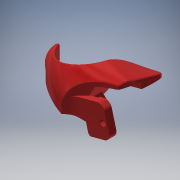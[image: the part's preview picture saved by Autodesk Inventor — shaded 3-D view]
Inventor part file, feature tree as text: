
AUTODESK INVENTOR PART (.ipt)
format: ipt  version: 2018 (Build 220112000, 112)  size: 882,688 bytes
history: native  units: mm
features: other x8, extrude x1, fillet x1, sketch x1, reference x1
ambient origin geometry x8: Origin, YZ Plane, XZ Plane, XY Plane, X Axis, Y Axis, Z Axis, Center Point
bodies: Body1 (feature_tree)
feature tree (12):
  other  "ソリッド1"
  other  "ダイレクト編集1"
  extrude  "押し出し1"  Depth=8.8365mm
  fillet  "フィレット1"  Radius=0.5mm
  sketch  "スケッチ1"
  reference  "参照1"
  other  "尺度1"
  other  "削除1"
  other  "削除2"
  parser-record x1  (decoder bookkeeping rows leaked as tree rows — omitted from the tree; the rows remain in map.json)
  other  "M-R-T.iam"
  other  "Servo_HK282A:1"
note: 1 file-system path scrubbed to <path> (originals preserved in map.json)
